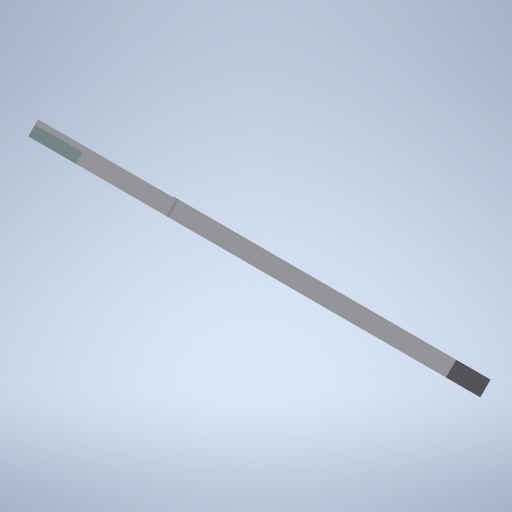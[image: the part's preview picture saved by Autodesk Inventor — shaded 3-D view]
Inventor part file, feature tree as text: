
AUTODESK INVENTOR PART (.ipt)
format: ipt  version: 2024.2 (Build 282272000, 272)  size: 474,624 bytes
history: native  units: in
note: dims shown in document units (in); Inventor stores cm internally (conversion verified against a paired STEP export)
features: extrude x12, sketch x3, other x2, chamfer x1, imported_body x1, projected_geometry x1
ambient origin geometry x8: Origin, YZ Plane, XZ Plane, XY Plane, X Axis, Y Axis, Z Axis, Center Point
bodies: Body1 (feature_tree)
feature tree (20):
  other  "product-name"
  other  "product-name1"
  extrude  "Extrusion1"  Depth=0.4in TaperAngle=0.0deg
  extrude  "Extrusion2"  Depth=0.4in TaperAngle=0.0deg
  extrude  "Extrusion3"  Depth=0.1772in
  extrude  "Extrusion4"  Depth=0.1772in TaperAngle=0.0deg
  extrude  "Extrusion5"  Depth=0.1772in TaperAngle=0.0deg
  extrude  "Extrusion7"  Depth=0.1772in TaperAngle=0.0deg
  extrude  "Extrusion8"  Depth=0.1772in TaperAngle=0.0deg
  extrude  "Extrusion9"  Depth=0.2454in TaperAngle=0.0deg
  extrude  "Extrusion10"  Depth=0.6693in
  extrude  "Extrusion11"  Depth=0.0787in
  extrude  "Extrusion12"  Depth=0.0787in
  chamfer  "Chamfer1"  Distance=2.4508in
  extrude  "Extrusion14"  Depth=0.12in TaperAngle=0.0deg
  imported_body  "Base1"
  sketch  "Sketch11"  dims[d0=1.0in d1=0.0in d2=0.4in d3=0.0in]
  sketch  "Sketch12"  dims[d4=0.4in d5=0.0in d6=0.4in d7=0.0in]
  sketch  "Sketch14"  dims[d8=0.2in d11=0.05in d12=0.4in d13=0.0in d16=1.0in d17=0.5in d18=0.0in d19=0.0in d20=0.45in d21=0.0in d22=0.45in d23=0.0in d24=0.2454in d25=0.0in d26=0.6693in d28=0.0787in d29=0.0787in d30=2.4508in d31=0.12in d32=0.0in d33=0.1772in d34=0.3543in d35=0.1969in d36=0.1772in d37=0.12in d38=0.0in d39=0.1969in d40=0.1969in d53=0.1575in d54=0.0787in d55=0.1374in d57=1.1417in d58=0.1004in d59=0.1969in d60=0.1772in d61=0.002in d62=0.002in d63=0.075in d64=0.0in d65=0.1969in d66=0.1772in d67=0.1969in d68=0.1772in]
  projected_geometry  "Projected Loop1"
